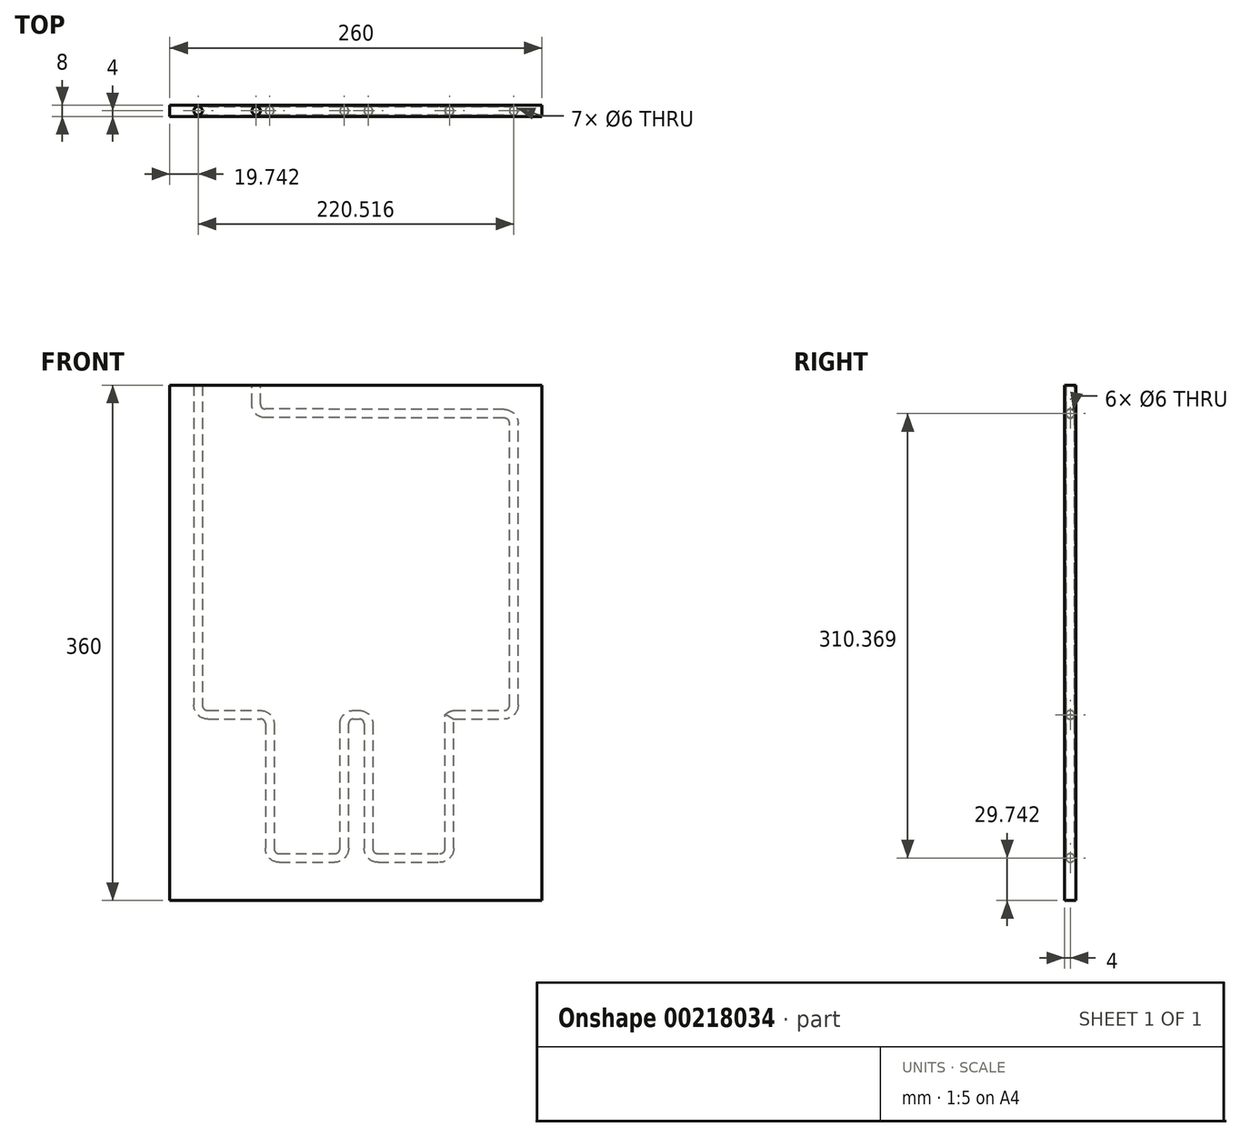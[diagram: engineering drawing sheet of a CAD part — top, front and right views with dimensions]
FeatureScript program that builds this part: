
annotation { "Feature Type Name" : "Feature", "Feature Type Description" : "" }
export const myFeature = defineFeature(function(context is Context, id is Id, definition is map)
    precondition{}
    {
        {
            var Q0;
            Q0=qCreatedBy(makeId("Front.planeOp"),FACE);
            var sketch = newSketch(context, id + "F0", { "sketchPlane" : qUnion([Q0])});
            skLineSegment(sketch, "E0.bottom", {"start": v(130, 180) * mm, "end": v(-130, 180) * mm});
            skLineSegment(sketch, "E0.top", {"start": v(130, -180) * mm, "end": v(-130, -180) * mm});
            skLineSegment(sketch, "E0.left", {"start": v(130, 180) * mm, "end": v(130, -180) * mm});
            skLineSegment(sketch, "E0.right", {"start": v(-130, 180) * mm, "end": v(-130, -180) * mm});
            skPoint(sketch, "E0.middle", {"position": v(0, 0) * mm});
            skSolve(sketch);
        }
        {
            var Q0;
            Q0=makeQuery(id+"F0.imprint","IMPRINT",FACE,{"disambiguationData":[TD([[makeQuery(id+"F0.imprint","IMPRINT",EDGE,{"derivedFrom":sQuery(id+"F0.wireOp",EDGE,"E0.bottom")}),1.0]])]});
            var sketch = newSketch(context, id + "F1", { "sketchPlane" : qUnion([Q0])});
            skLineSegment(sketch, "E1", {"start": v(-110, 200) * mm, "end": v(-110, -43.5) * mm});
            skLineSegment(sketch, "E2", {"start": v(-70, 200) * mm, "end": v(-70, 166.49) * mm});
            skLineSegment(sketch, "E3", {"start": v(-103.5, -50) * mm, "end": v(-66.5, -50) * mm});
            skLineSegment(sketch, "E4", {"start": v(69.14, -50) * mm, "end": v(103.5, -50) * mm});
            skLineSegment(sketch, "E5", {"start": v(110, -43.5) * mm, "end": v(110, 153.21) * mm});
            skLineSegment(sketch, "E6", {"start": v(103.51, 159.71) * mm, "end": v(-63.51, 159.99) * mm});
            skPoint(sketch, "E7.visualSharp", {"position": v(-110, -50) * mm});
            skArc(sketch, "E7.filletArc", {"start": v(-110, -43.5) * mm, "mid": v(-108.1, -48.1) * mm, "end": v(-103.5, -50) * mm});
            skPoint(sketch, "E8.visualSharp", {"position": v(-60, -50) * mm});
            skArc(sketch, "E8.filletArc", {"start": v(-60, -56.5) * mm, "mid": v(-61.9, -51.9) * mm, "end": v(-66.5, -50) * mm});
            skPoint(sketch, "E9.visualSharp", {"position": v(-60, -150) * mm});
            skPoint(sketch, "E10.visualSharp", {"position": v(60, -50) * mm});
            skArc(sketch, "E10.filletArc", {"start": v(69.14, -50) * mm, "mid": v(66.97, -50.37) * mm, "end": v(65.05, -51.45) * mm});
            skPoint(sketch, "E11.visualSharp", {"position": v(110, -50) * mm});
            skArc(sketch, "E11.filletArc", {"start": v(103.5, -50) * mm, "mid": v(108.1, -48.1) * mm, "end": v(110, -43.5) * mm});
            skPoint(sketch, "E12.visualSharp", {"position": v(110, 159.7) * mm});
            skArc(sketch, "E12.filletArc", {"start": v(110, 153.21) * mm, "mid": v(108.1, 157.8) * mm, "end": v(103.51, 159.71) * mm});
            skPoint(sketch, "E13.visualSharp", {"position": v(-70, 160) * mm});
            skArc(sketch, "E13.filletArc", {"start": v(-70, 166.49) * mm, "mid": v(-68.1, 161.9) * mm, "end": v(-63.51, 159.99) * mm});
            skLineSegment(sketch, "E14", {"start": v(-8.43, -143.5) * mm, "end": v(-8.43, -56.5) * mm});
            skLineSegment(sketch, "E15", {"start": v(-1.93, -50) * mm, "end": v(2.45, -50) * mm});
            skLineSegment(sketch, "E16", {"start": v(8.95, -56.5) * mm, "end": v(8.95, -143.5) * mm});
            skPoint(sketch, "E17.visualSharp", {"position": v(-8.43, -150) * mm});
            skArc(sketch, "E17.filletArc", {"start": v(-14.93, -150) * mm, "mid": v(-10.33, -148.1) * mm, "end": v(-8.43, -143.5) * mm});
            skPoint(sketch, "E18.visualSharp", {"position": v(-8.43, -50) * mm});
            skArc(sketch, "E18.filletArc", {"start": v(-1.93, -50) * mm, "mid": v(-6.52, -51.9) * mm, "end": v(-8.43, -56.5) * mm});
            skPoint(sketch, "E19.visualSharp", {"position": v(8.95, -50) * mm});
            skArc(sketch, "E19.filletArc", {"start": v(8.95, -56.5) * mm, "mid": v(7.05, -51.9) * mm, "end": v(2.45, -50) * mm});
            skPoint(sketch, "E20.visualSharp", {"position": v(8.95, -150) * mm});
            skArc(sketch, "E20.filletArc", {"start": v(8.95, -143.5) * mm, "mid": v(10.85, -148.1) * mm, "end": v(15.45, -150) * mm});
            skLineSegment(sketch, "E21", {"start": v(15.45, -150) * mm, "end": v(58.55, -150) * mm});
            skLineSegment(sketch, "E22", {"start": v(65.05, -143.5) * mm, "end": v(65.05, -51.45) * mm});
            skPoint(sketch, "E23.visualSharp", {"position": v(65.05, -150) * mm});
            skArc(sketch, "E23.filletArc", {"start": v(58.55, -150) * mm, "mid": v(63.15, -148.1) * mm, "end": v(65.05, -143.5) * mm});
            skLineSegment(sketch, "E24", {"start": v(-14.93, -150) * mm, "end": v(-53.5, -150) * mm});
            skLineSegment(sketch, "E25", {"start": v(-60, -143.5) * mm, "end": v(-60, -56.5) * mm});
            skArc(sketch, "E26.filletArc", {"start": v(-60, -143.5) * mm, "mid": v(-58.1, -148.1) * mm, "end": v(-53.5, -150) * mm});
            skSolve(sketch);
        }
        {
            var Q0;
            Q0=makeQuery(id+"F0.imprint","IMPRINT",FACE,{"disambiguationData":[TD([[makeQuery(id+"F0.imprint","IMPRINT",EDGE,{"derivedFrom":sQuery(id+"F0.wireOp",EDGE,"E0.bottom")}),1.0]])]});
            extrude(context, id + "F2", {"entities" : qUnion([Q0]), "depth" : 8 * mm, "symmetric" : true});
        }
        {
            var Q0;
            Q0=sQuery(id+"F1.wireOp",VERTEX,"E1.start");
            var Q1;
            Q1=qCreatedBy(makeId("Top.planeOp"),FACE);
            cPlane(context, id + "F3", {"entities" : qUnion([Q0, Q1]), "cplaneType" : CPlaneType.PLANE_POINT, "offset" : 25 * mm, "width" : 150 * mm, "height" : 150 * mm});
        }
        {
            var Q0;
            Q0=qCreatedBy(id+"F3.planeOp",FACE);
            var sketch = newSketch(context, id + "F4", { "sketchPlane" : qUnion([Q0])});
            skCircle(sketch, "E27", {"center": v(-110.26, 0) * mm, "radius": 3 * mm});
            skCircle(sketch, "E28", {"center": v(-70.07, 0) * mm, "radius": 3 * mm});
            skSolve(sketch);
        }
        {
            var Q0;
            Q0=makeQuery(id+"F4.imprint","IMPRINT",FACE,{"disambiguationData":[TD([[makeQuery(id+"F4.imprint","IMPRINT",EDGE,{"derivedFrom":sQuery(id+"F4.wireOp",EDGE,"E27")}),1.0]])]});
            var Q1;
            Q1=sQuery(id+"F1.wireOp",EDGE,"E1");
            var Q2;
            Q2=sQuery(id+"F1.wireOp",EDGE,"E7.filletArc");
            var Q3;
            Q3=sQuery(id+"F1.wireOp",EDGE,"E3");
            var Q4;
            Q4=sQuery(id+"F1.wireOp",EDGE,"E8.filletArc");
            var Q5;
            Q5=sQuery(id+"F1.wireOp",EDGE,"E25");
            var Q6;
            Q6=sQuery(id+"F1.wireOp",EDGE,"E26.filletArc");
            var Q7;
            Q7=sQuery(id+"F1.wireOp",EDGE,"E24");
            var Q8;
            Q8=sQuery(id+"F1.wireOp",EDGE,"E17.filletArc");
            var Q9;
            Q9=sQuery(id+"F1.wireOp",EDGE,"E14");
            var Q10;
            Q10=sQuery(id+"F1.wireOp",EDGE,"E18.filletArc");
            var Q11;
            Q11=sQuery(id+"F1.wireOp",EDGE,"E15");
            var Q12;
            Q12=sQuery(id+"F1.wireOp",EDGE,"E19.filletArc");
            var Q13;
            Q13=sQuery(id+"F1.wireOp",EDGE,"E16");
            var Q14;
            Q14=sQuery(id+"F1.wireOp",EDGE,"E20.filletArc");
            var Q15;
            Q15=sQuery(id+"F1.wireOp",EDGE,"E21");
            var Q16;
            Q16=sQuery(id+"F1.wireOp",EDGE,"E23.filletArc");
            var Q17;
            Q17=sQuery(id+"F1.wireOp",EDGE,"E22");
            var Q18;
            Q18=sQuery(id+"F1.wireOp",EDGE,"E4");
            var Q19;
            Q19=sQuery(id+"F1.wireOp",EDGE,"E10.filletArc");
            var Q20;
            Q20=sQuery(id+"F1.wireOp",EDGE,"E11.filletArc");
            var Q21;
            Q21=sQuery(id+"F1.wireOp",EDGE,"E5");
            var Q22;
            Q22=sQuery(id+"F1.wireOp",EDGE,"E12.filletArc");
            var Q23;
            Q23=sQuery(id+"F1.wireOp",EDGE,"E6");
            var Q24;
            Q24=sQuery(id+"F1.wireOp",EDGE,"E13.filletArc");
            var Q25;
            Q25=sQuery(id+"F1.wireOp",EDGE,"E2");
            sweep(context, id + "F5", {"operationType" : NewBodyOperationType.REMOVE, "profiles" : qUnion([Q0]), "path" : qUnion([Q1, Q2, Q3, Q4, Q5, Q6, Q7, Q8, Q9, Q10, Q11, Q12, Q13, Q14, Q15, Q16, Q17, Q18, Q19, Q20, Q21, Q22, Q23, Q24, Q25])});
        }
    });
